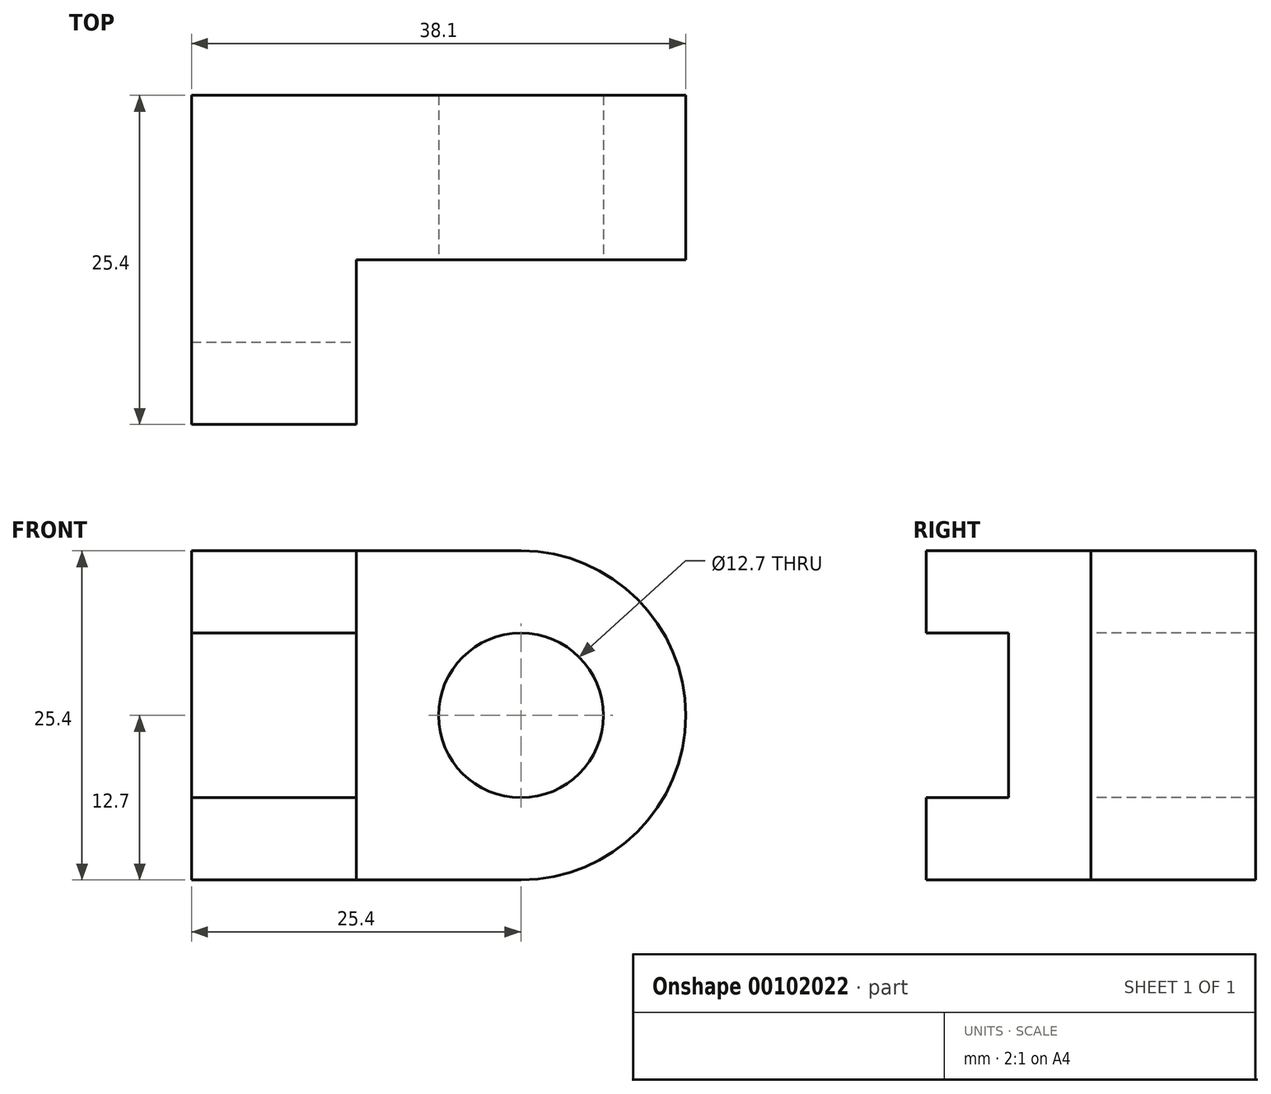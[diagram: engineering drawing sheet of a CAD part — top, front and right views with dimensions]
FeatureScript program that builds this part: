
annotation { "Feature Type Name" : "Feature", "Feature Type Description" : "" }
export const myFeature = defineFeature(function(context is Context, id is Id, definition is map)
    precondition{}
    {
        {
            var Q0;
            Q0=qCreatedBy(makeId("Top.planeOp"),FACE);
            var sketch = newSketch(context, id + "F0", { "sketchPlane" : qUnion([Q0])});
            skLineSegment(sketch, "E0", {"start": v(0, 0) * mm, "end": v(12.7, 0) * mm});
            skLineSegment(sketch, "E1", {"start": v(12.7, 0) * mm, "end": v(12.7, 12.7) * mm});
            skLineSegment(sketch, "E2", {"start": v(12.7, 12.7) * mm, "end": v(25.4, 12.7) * mm});
            skLineSegment(sketch, "E3", {"start": v(25.4, 12.7) * mm, "end": v(25.4, 25.4) * mm});
            skLineSegment(sketch, "E4", {"start": v(25.4, 25.4) * mm, "end": v(0, 25.4) * mm});
            skLineSegment(sketch, "E5", {"start": v(0, 25.4) * mm, "end": v(0, 0) * mm});
            skSolve(sketch);
        }
        {
            var Q0;
            Q0 = qSketchRegion(id + "F0", true);
            extrude(context, id + "F1", {"entities" : qUnion([Q0]), "depth" : 25.4 * mm});
        }
        {
            var Q0;
            Q0=makeQuery(id+"F1.opExtrude","SWEPT_FACE",FACE,{"disambiguationData":[OSD([sQuery(id+"F0.wireOp",EDGE,"E0")])]});
            var sketch = newSketch(context, id + "F2", { "sketchPlane" : qUnion([Q0])});
            skLineSegment(sketch, "E6", {"start": v(0, 0) * mm, "end": v(0, 6.35) * mm});
            skLineSegment(sketch, "E7", {"start": v(0, 6.35) * mm, "end": v(12.7, 6.35) * mm});
            skLineSegment(sketch, "E8", {"start": v(12.7, 6.35) * mm, "end": v(12.7, 0) * mm});
            skLineSegment(sketch, "E9", {"start": v(0, 25.4) * mm, "end": v(0, 19.05) * mm});
            skLineSegment(sketch, "E10", {"start": v(0, 19.05) * mm, "end": v(12.7, 19.05) * mm});
            skLineSegment(sketch, "E11", {"start": v(12.7, 19.05) * mm, "end": v(12.7, 25.4) * mm});
            skSolve(sketch);
        }
        {
            var Q0;
            {var subQ0=sQuery(id+"F2.wireOp",EDGE,"E7");Q0=makeQuery(id+"F2.imprint","IMPRINT",FACE,{"disambiguationData":[TD([[makeQuery(id+"F2.imprint","IMPRINT",EDGE,{"derivedFrom":subQ0}),1.0]])]});}
            extrude(context, id + "F3", {"entities" : qUnion([Q0]), "operationType" : NewBodyOperationType.REMOVE, "oppositeDirection" : true, "depth" : 6.35 * mm});
        }
        {
            var Q0;
            Q0=makeQuery(id+"F1.opExtrude","SWEPT_FACE",FACE,{"disambiguationData":[OSD([sQuery(id+"F0.wireOp",EDGE,"E4")])]});
            var sketch = newSketch(context, id + "F4", { "sketchPlane" : qUnion([Q0])});
            skArc(sketch, "E12", {"start": v(-25.4, 25.4) * mm, "mid": v(-38.1, 12.7) * mm, "end": v(-25.4, 0) * mm});
            skSolve(sketch);
        }
        {
            var Q0;
            Q0=makeQuery(id+"F4.imprint","IMPRINT",FACE,{"disambiguationData":[TD([[makeQuery(id+"F4.imprint","IMPRINT",EDGE,{"derivedFrom":sQuery(id+"F4.wireOp",EDGE,"E12")}),1.0]])]});
            extrude(context, id + "F5", {"entities" : qUnion([Q0]), "operationType" : NewBodyOperationType.ADD, "oppositeDirection" : true, "depth" : 12.7 * mm});
        }
        {
            var Q0;
            Q0=makeQuery(id+"F5.boolean.opBoolean","MERGE",FACE,{"derivedFrom":[makeQuery(id+"F1.opExtrude","SWEPT_FACE",FACE,{"disambiguationData":[OSD([sQuery(id+"F0.wireOp",EDGE,"E2")])]}),makeQuery(id+"F5.opExtrude","CAP_FACE",FACE,{"disambiguationData":[OSD([sQuery(id+"F0.wireOp",EDGE,"E3"),sQuery(id+"F0.wireOp",EDGE,"E4"),sQuery(id+"F4.wireOp",EDGE,"E12")])],"isStart":false})]});
            var sketch = newSketch(context, id + "F6", { "sketchPlane" : qUnion([Q0])});
            skCircle(sketch, "E13", {"center": v(25.4, 12.7) * mm, "radius": 6.35 * mm});
            skSolve(sketch);
        }
        {
            var Q0;
            Q0=makeQuery(id+"F6.imprint","IMPRINT",FACE,{"disambiguationData":[TD([[makeQuery(id+"F6.imprint","IMPRINT",EDGE,{"derivedFrom":sQuery(id+"F6.wireOp",EDGE,"E13")}),1.0]])]});
            extrude(context, id + "F7", {"entities" : qUnion([Q0]), "operationType" : NewBodyOperationType.REMOVE, "oppositeDirection" : true, "depth" : 12.7 * mm});
        }
    });
